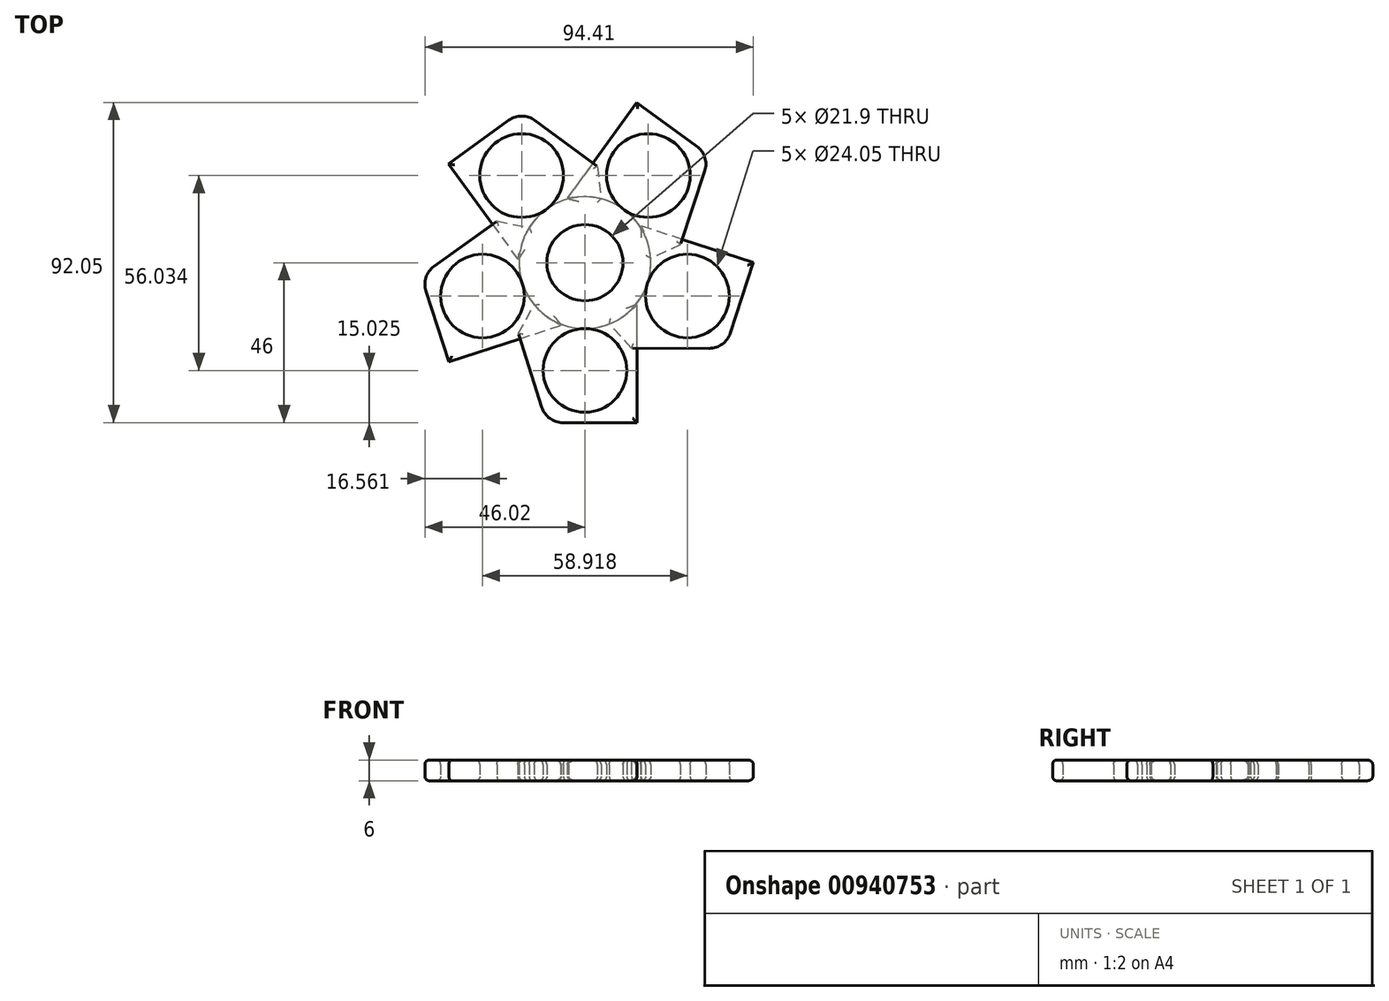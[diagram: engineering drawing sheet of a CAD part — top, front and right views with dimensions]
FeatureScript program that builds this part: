
annotation { "Feature Type Name" : "Feature", "Feature Type Description" : "" }
export const myFeature = defineFeature(function(context is Context, id is Id, definition is map)
    precondition{}
    {
        {
            var Q0;
            Q0=qCreatedBy(makeId("Top.planeOp"),FACE);
            var sketch = newSketch(context, id + "F0", { "sketchPlane" : qUnion([Q0])});
            skCircle(sketch, "E0", {"center": v(0, 0) * mm, "radius": 18.95 * mm});
            skCircle(sketch, "E1", {"center": v(0, 0) * mm, "radius": 10.95 * mm});
            skSolve(sketch);
        }
        {
            var Q0;
            Q0=makeQuery(id+"F0.imprint","IMPRINT",FACE,{"disambiguationData":[TD([[makeQuery(id+"F0.imprint","IMPRINT",EDGE,{"derivedFrom":sQuery(id+"F0.wireOp",EDGE,"E1")}),-1.0]])]});
            extrude(context, id + "F1", {"entities" : qUnion([Q0]), "depth" : 6 * mm, "offsetDistance" : 25.4 * mm});
        }
        {
            var Q0;
            Q0=makeQuery(id+"F0.imprint","IMPRINT",FACE,{"disambiguationData":[TD([[makeQuery(id+"F0.imprint","IMPRINT",EDGE,{"derivedFrom":sQuery(id+"F0.wireOp",EDGE,"E1")}),1.0]])]});
            var sketch = newSketch(context, id + "F2", { "sketchPlane" : qUnion([Q0])});
            skCircle(sketch, "E2", {"center": v(0, -30.98) * mm, "radius": 12.03 * mm});
            skLineSegment(sketch, "E3", {"start": v(-19.17, -20.32) * mm, "end": v(-12.39, -41.58) * mm});
            skLineSegment(sketch, "E4", {"start": v(-6.34, -46) * mm, "end": v(15.03, -46) * mm});
            skLineSegment(sketch, "E5", {"start": v(15.03, -46) * mm, "end": v(15.03, -12.1) * mm});
            skPoint(sketch, "E6.visualSharp", {"position": v(-10.98, -46) * mm});
            skArc(sketch, "E6.filletArc", {"start": v(-12.39, -41.58) * mm, "mid": v(-10.09, -44.78) * mm, "end": v(-6.34, -46) * mm});
            skLineSegment(sketch, "E7", {"start": v(-13.69, -10.56) * mm, "end": v(15.03, -12.1) * mm});
            skLineSegment(sketch, "E8", {"start": v(-19.17, -20.32) * mm, "end": v(-13.69, -10.56) * mm});
            skSolve(sketch);
        }
        {
            var Q0;
            Q0=makeQuery(id+"F2.imprint","IMPRINT",FACE,{"disambiguationData":[TD([[makeQuery(id+"F2.imprint","IMPRINT",EDGE,{"derivedFrom":sQuery(id+"F2.wireOp",EDGE,"06lBKKmj-HHmP-qTi7-cT2x-EhQSNvDSQOlI")}),1.0]])]});
            var Q1;
            Q1=makeQuery(id+"F2.imprint","IMPRINT",FACE,{"disambiguationData":[TD([[makeQuery(id+"F2.imprint","IMPRINT",EDGE,{"derivedFrom":sQuery(id+"F2.wireOp",EDGE,"E3")}),1.0]])]});
            extrude(context, id + "F3", {"entities" : qUnion([Q0, Q1]), "operationType" : NewBodyOperationType.ADD, "depth" : 6 * mm, "offsetDistance" : 25.4 * mm});
        }
        {
            var Q0;
            Q0=makeQuery(id+"F6.opPattern","COPY",EDGE,{"derivedFrom":makeQuery(id+"F3.opExtrude","CAP_EDGE",EDGE,{"disambiguationData":[OSD([sQuery(id+"F2.wireOp",EDGE,"E3")])],"isStart":false}),"instanceName":"1"});
            var Q1;
            Q1=makeQuery(id+"F6.opPattern","COPY",EDGE,{"derivedFrom":makeQuery(id+"F3.opExtrude","CAP_EDGE",EDGE,{"disambiguationData":[OSD([sQuery(id+"F2.wireOp",EDGE,"E5")])],"isStart":false}),"instanceName":"1"});
            var Q2;
            Q2=makeQuery(id+"F6.opPattern","COPY",EDGE,{"derivedFrom":makeQuery(id+"F3.opExtrude","CAP_EDGE",EDGE,{"disambiguationData":[OSD([sQuery(id+"F2.wireOp",EDGE,"E3")])],"isStart":false}),"instanceName":"2"});
            var Q3;
            Q3=makeQuery(id+"F6.opPattern","COPY",EDGE,{"derivedFrom":makeQuery(id+"F3.opExtrude","CAP_EDGE",EDGE,{"disambiguationData":[OSD([sQuery(id+"F2.wireOp",EDGE,"E3")])],"isStart":false}),"instanceName":"3"});
            var Q4;
            Q4=makeQuery(id+"F6.opPattern","COPY",EDGE,{"derivedFrom":makeQuery(id+"F3.opExtrude","CAP_EDGE",EDGE,{"disambiguationData":[OSD([sQuery(id+"F2.wireOp",EDGE,"E5")])],"isStart":false}),"instanceName":"3"});
            var Q5;
            Q5=makeQuery(id+"F6.opPattern","COPY",EDGE,{"derivedFrom":makeQuery(id+"F3.opExtrude","CAP_EDGE",EDGE,{"disambiguationData":[OSD([sQuery(id+"F2.wireOp",EDGE,"E5")])],"isStart":false}),"instanceName":"4"});
            var Q6;
            Q6=makeQuery(id+"F6.opPattern","COPY",EDGE,{"derivedFrom":makeQuery(id+"F3.opExtrude","CAP_EDGE",EDGE,{"disambiguationData":[OSD([sQuery(id+"F2.wireOp",EDGE,"E3")])],"isStart":false}),"instanceName":"4"});
            var Q7;
            Q7=makeQuery(id+"F6.opPattern","COPY",EDGE,{"derivedFrom":makeQuery(id+"F3.opExtrude","CAP_EDGE",EDGE,{"disambiguationData":[OSD([sQuery(id+"F2.wireOp",EDGE,"E5")])],"isStart":false}),"instanceName":"2"});
            var Q8;
            {var subQ0=sQuery(id+"F0.wireOp",EDGE,"E1");Q8=makeQuery(id+"F3.boolean.opBoolean","MERGE",FACE,{"derivedFrom":[makeQuery(id+"F1.opExtrude","CAP_FACE",FACE,{"disambiguationData":[OSD([sQuery(id+"F0.wireOp",EDGE,"E0"),subQ0])],"isStart":false}),makeQuery(id+"F3.opExtrude","CAP_FACE",FACE,{"disambiguationData":[OSD([subQ0,sQuery(id+"F2.wireOp",EDGE,"E2"),sQuery(id+"F2.wireOp",EDGE,"E3"),sQuery(id+"F2.wireOp",EDGE,"E4"),sQuery(id+"F2.wireOp",EDGE,"E5"),sQuery(id+"F2.wireOp",EDGE,"E6.filletArc"),sQuery(id+"F2.wireOp",EDGE,"E7")])],"isStart":false})]});}
            fillet(context, id + "F4", {"entities" : qUnion([Q0, Q1, Q2, Q3, Q4, Q5, Q6, Q7, Q8]), "radius" : 1.27 * mm, "tangentPropagation" : true, "allowEdgeOverflow" : false});
        }
        {
            var Q0;
            {var subQ0=sQuery(id+"F0.wireOp",EDGE,"E1");Q0=makeQuery(id+"F6.opPattern","COPY",FACE,{"derivedFrom":makeQuery(id+"F3.boolean.opBoolean","MERGE",FACE,{"derivedFrom":[makeQuery(id+"F1.opExtrude","CAP_FACE",FACE,{"disambiguationData":[OSD([sQuery(id+"F0.wireOp",EDGE,"E0"),subQ0])],"isStart":true}),makeQuery(id+"F3.opExtrude","CAP_FACE",FACE,{"disambiguationData":[OSD([subQ0,sQuery(id+"F2.wireOp",EDGE,"E2"),sQuery(id+"F2.wireOp",EDGE,"E3"),sQuery(id+"F2.wireOp",EDGE,"E4"),sQuery(id+"F2.wireOp",EDGE,"E5"),sQuery(id+"F2.wireOp",EDGE,"E6.filletArc"),sQuery(id+"F2.wireOp",EDGE,"E7")])],"isStart":true})]}),"instanceName":"3"});}
            var Q1;
            {var subQ0=sQuery(id+"F0.wireOp",EDGE,"E1");Q1=makeQuery(id+"F3.boolean.opBoolean","MERGE",FACE,{"derivedFrom":[makeQuery(id+"F1.opExtrude","CAP_FACE",FACE,{"disambiguationData":[OSD([sQuery(id+"F0.wireOp",EDGE,"E0"),subQ0])],"isStart":true}),makeQuery(id+"F3.opExtrude","CAP_FACE",FACE,{"disambiguationData":[OSD([subQ0,sQuery(id+"F2.wireOp",EDGE,"E2"),sQuery(id+"F2.wireOp",EDGE,"E3"),sQuery(id+"F2.wireOp",EDGE,"E4"),sQuery(id+"F2.wireOp",EDGE,"E5"),sQuery(id+"F2.wireOp",EDGE,"E6.filletArc"),sQuery(id+"F2.wireOp",EDGE,"E7")])],"isStart":true})]});}
            fillet(context, id + "F5", {"entities" : qUnion([Q0, Q1]), "radius" : 1.27 * mm, "tangentPropagation" : true, "allowEdgeOverflow" : false});
        }
        {
            var Q0;
            Q0=makeQuery(id+"F1.opExtrude","SWEPT_BODY",BODY,{"disambiguationData":[OSD([sQuery(id+"F0.wireOp",EDGE,"E0"),sQuery(id+"F0.wireOp",EDGE,"E1")])]});
            var Q1;
            Q1=sQuery(id+"F0.wireOp",EDGE,"E1");
            circularPattern(context, id + "F6", {"entities" : qUnion([Q0]), "axis" : qUnion([Q1]), "angle" : 360 * degree, "instanceCount" : 5, "equalSpace" : true});
        }
    });
